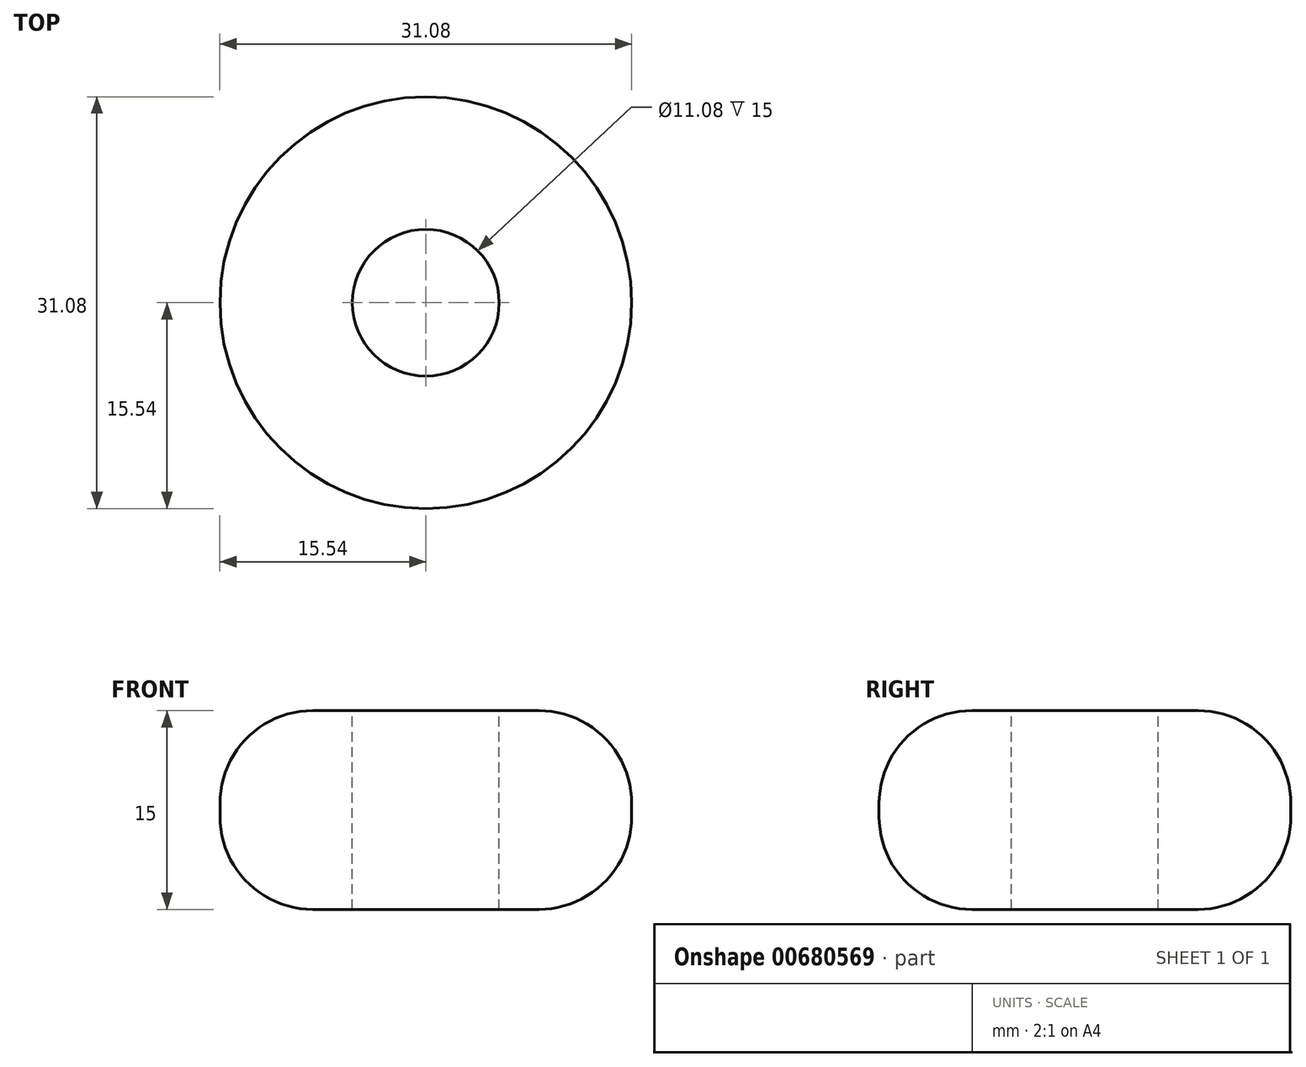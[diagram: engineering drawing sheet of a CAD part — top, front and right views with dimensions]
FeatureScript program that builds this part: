
annotation { "Feature Type Name" : "Feature", "Feature Type Description" : "" }
export const myFeature = defineFeature(function(context is Context, id is Id, definition is map)
    precondition{}
    {
        {
            var Q0;
            Q0=qCreatedBy(makeId("Front.planeOp"),FACE);
            var sketch = newSketch(context, id + "F0", { "sketchPlane" : qUnion([Q0])});
            skLineSegment(sketch, "E0", {"start": v(0, 14.97) * mm, "end": v(0, -18.89) * mm, "construction": true});
            skLineSegment(sketch, "E1.bottom", {"start": v(5.54, 0.73) * mm, "end": v(15.54, 0.73) * mm});
            skLineSegment(sketch, "E1.top", {"start": v(5.54, -14.27) * mm, "end": v(15.54, -14.27) * mm});
            skLineSegment(sketch, "E1.left", {"start": v(5.54, 0.73) * mm, "end": v(5.54, -14.27) * mm});
            skLineSegment(sketch, "E1.right", {"start": v(15.54, 0.73) * mm, "end": v(15.54, -14.27) * mm});
            skSolve(sketch);
        }
        {
            var Q0;
            Q0=makeQuery(id+"F0.imprint","IMPRINT",FACE,{"disambiguationData":[TD([[makeQuery(id+"F0.imprint","IMPRINT",EDGE,{"derivedFrom":sQuery(id+"F0.wireOp",EDGE,"E1.bottom")}),-1.0]])]});
            var Q1;
            Q1=sQuery(id+"F0.wireOp",EDGE,"E0");
            revolve(context, id + "F1", {"surfaceOperationType" : NewSurfaceOperationType.NEW, "entities" : qUnion([Q0]), "axis" : qUnion([Q1]), "revolveType" : RevolveType.FULL});
        }
        {
            var Q0;
            Q0=makeQuery(id+"F1.opRevolve","SWEPT_EDGE",EDGE,{"disambiguationData":[OSD([sQuery(id+"F0.wireOp",EDGE,"E1.bottom"),sQuery(id+"F0.wireOp",EDGE,"E1.right")])]});
            var Q1;
            Q1=makeQuery(id+"F1.opRevolve","SWEPT_EDGE",EDGE,{"disambiguationData":[OSD([sQuery(id+"F0.wireOp",EDGE,"E1.top"),sQuery(id+"F0.wireOp",EDGE,"E1.right")])]});
            fillet(context, id + "F2", {"entities" : qUnion([Q0, Q1]), "radius" : 7 * mm, "tangentPropagation" : true, "allowEdgeOverflow" : false});
        }
    });
